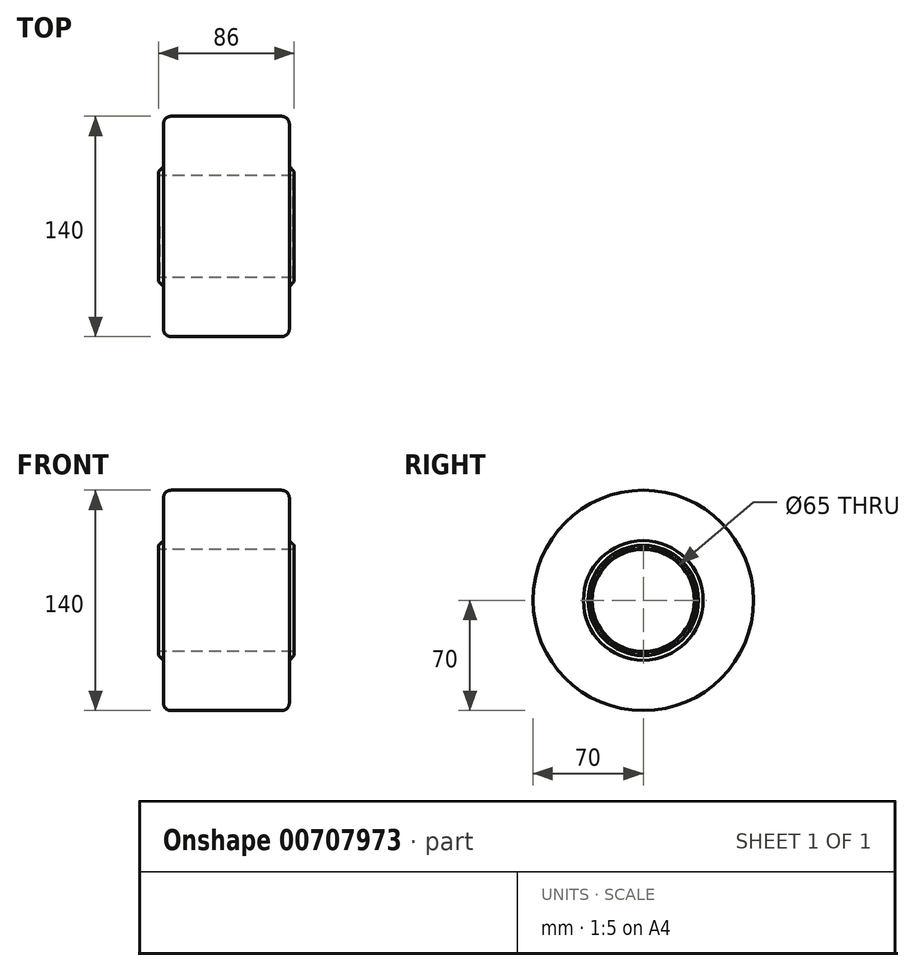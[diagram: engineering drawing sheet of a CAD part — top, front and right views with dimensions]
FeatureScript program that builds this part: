
annotation { "Feature Type Name" : "Feature", "Feature Type Description" : "" }
export const myFeature = defineFeature(function(context is Context, id is Id, definition is map)
    precondition{}
    {
        {
            var Q0;
            Q0=qCreatedBy(makeId("Front.planeOp"),FACE);
            var sketch = newSketch(context, id + "F0", { "sketchPlane" : qUnion([Q0])});
            skLineSegment(sketch, "E0", {"start": v(-43, 32.5) * mm, "end": v(43, 32.5) * mm});
            skLineSegment(sketch, "E1", {"start": v(43, 32.5) * mm, "end": v(43, 35) * mm});
            skLineSegment(sketch, "E2", {"start": v(43, 35) * mm, "end": v(40, 38) * mm});
            skLineSegment(sketch, "E3", {"start": v(40, 38) * mm, "end": v(40, 70) * mm});
            skLineSegment(sketch, "E4", {"start": v(40, 70) * mm, "end": v(-40, 70) * mm});
            skLineSegment(sketch, "E5", {"start": v(-40, 70) * mm, "end": v(-40, 38) * mm});
            skLineSegment(sketch, "E6", {"start": v(-40, 38) * mm, "end": v(-43, 35) * mm});
            skLineSegment(sketch, "E7", {"start": v(-43, 35) * mm, "end": v(-43, 32.5) * mm});
            skLineSegment(sketch, "E8", {"start": v(-55.66, 0) * mm, "end": v(77.12, 0) * mm});
            skSolve(sketch);
        }
        {
            var Q0;
            Q0=makeQuery(id+"F0.imprint","IMPRINT",FACE,{"disambiguationData":[TD([[makeQuery(id+"F0.imprint","IMPRINT",EDGE,{"derivedFrom":sQuery(id+"F0.wireOp",EDGE,"E0")}),1.0]])]});
            var Q1;
            Q1=sQuery(id+"F0.wireOp",EDGE,"E8");
            revolve(context, id + "F1", {"surfaceOperationType" : NewSurfaceOperationType.NEW, "entities" : qUnion([Q0]), "axis" : qUnion([Q1]), "revolveType" : RevolveType.FULL});
        }
        {
            var Q0;
            Q0=makeQuery(id+"F1.opRevolve","SWEPT_EDGE",EDGE,{"disambiguationData":[OSD([sQuery(id+"F0.wireOp",EDGE,"E4"),sQuery(id+"F0.wireOp",EDGE,"E5")])]});
            var Q1;
            Q1=makeQuery(id+"F1.opRevolve","SWEPT_EDGE",EDGE,{"disambiguationData":[OSD([sQuery(id+"F0.wireOp",EDGE,"E3"),sQuery(id+"F0.wireOp",EDGE,"E4")])]});
            fillet(context, id + "F2", {"entities" : qUnion([Q0, Q1]), "radius" : 5 * mm, "tangentPropagation" : true, "allowEdgeOverflow" : false});
        }
        {
            var Q0;
            Q0=makeQuery(id+"F1.opRevolve","SWEPT_EDGE",EDGE,{"disambiguationData":[OSD([sQuery(id+"F0.wireOp",EDGE,"E0"),sQuery(id+"F0.wireOp",EDGE,"E7")])]});
            var Q1;
            Q1=makeQuery(id+"F1.opRevolve","SWEPT_FACE",FACE,{"disambiguationData":[OSD([sQuery(id+"F0.wireOp",EDGE,"E0")])]});
            chamfer(context, id + "F3", {"entities" : qUnion([Q0, Q1]), "width" : 0.5 * mm, "tangentPropagation" : true});
        }
    });
